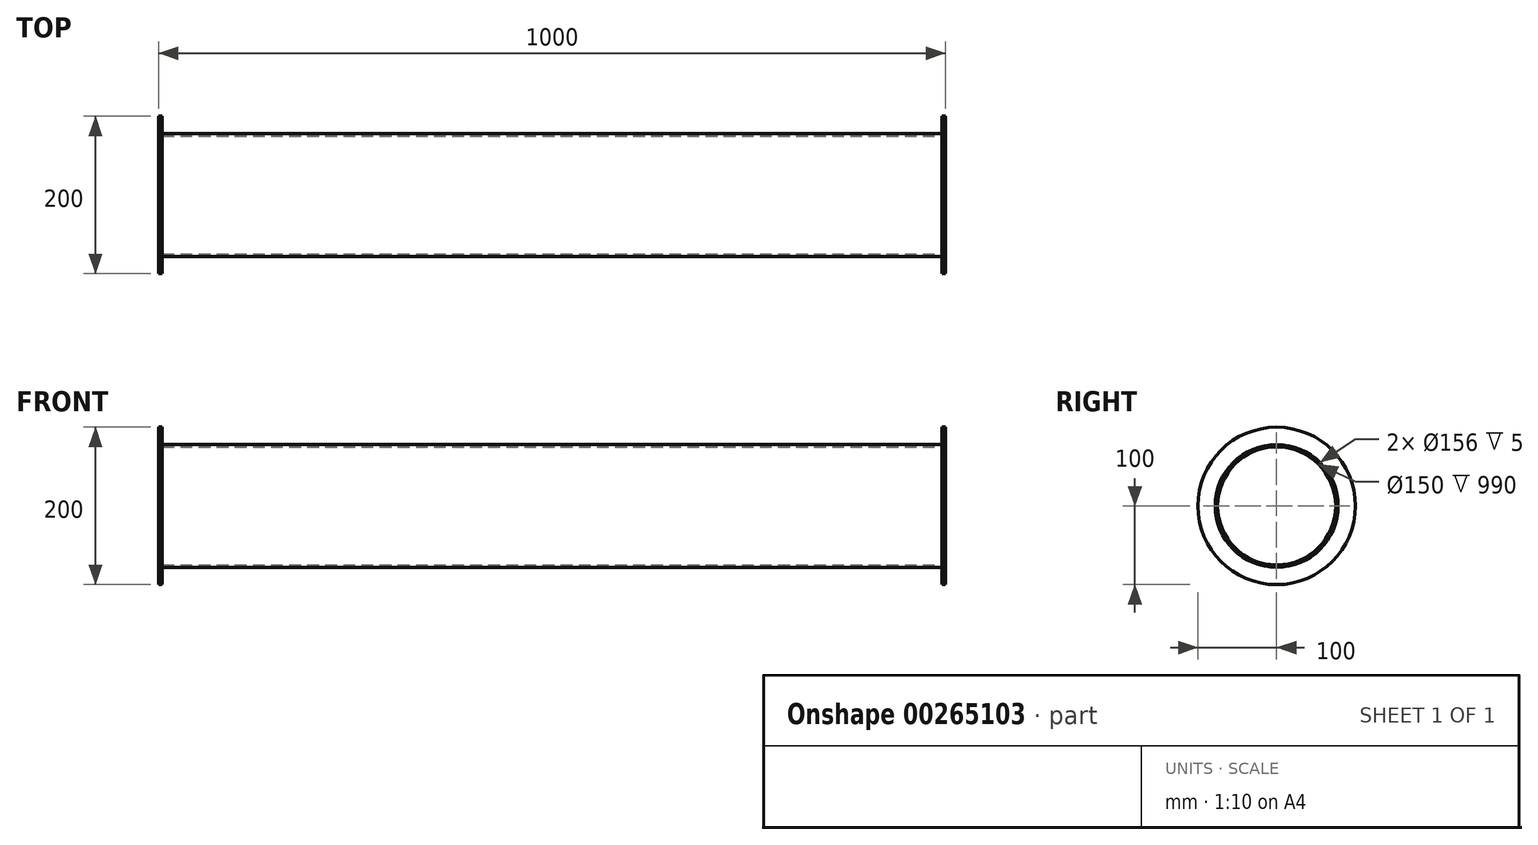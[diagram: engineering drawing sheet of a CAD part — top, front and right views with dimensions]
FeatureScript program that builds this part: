
annotation { "Feature Type Name" : "Feature", "Feature Type Description" : "" }
export const myFeature = defineFeature(function(context is Context, id is Id, definition is map)
    precondition{}
    {
        {
            var Q0;
            Q0=qCreatedBy(makeId("Front.planeOp"),FACE);
            var sketch = newSketch(context, id + "F0", { "sketchPlane" : qUnion([Q0])});
            skLineSegment(sketch, "E0", {"start": v(0, 0) * mm, "end": v(-990, 0) * mm, "construction": true});
            skLineSegment(sketch, "E1.bottom", {"start": v(0, 75) * mm, "end": v(-990, 75) * mm});
            skLineSegment(sketch, "E1.top", {"start": v(0, 78) * mm, "end": v(-990, 78) * mm});
            skLineSegment(sketch, "E1.left", {"start": v(0, 75) * mm, "end": v(0, 78) * mm});
            skLineSegment(sketch, "E1.right", {"start": v(-990, 75) * mm, "end": v(-990, 78) * mm});
            skSolve(sketch);
        }
        {
            var Q0;
            Q0=makeQuery(id+"F0.imprint","IMPRINT",FACE,{"disambiguationData":[TD([[makeQuery(id+"F0.imprint","IMPRINT",EDGE,{"derivedFrom":sQuery(id+"F0.wireOp",EDGE,"E1.bottom")}),-1.0]])]});
            var Q1;
            Q1=sQuery(id+"F0.wireOp",EDGE,"E0");
            revolve(context, id + "F1", {"entities" : qUnion([Q0]), "axis" : qUnion([Q1]), "revolveType" : RevolveType.FULL});
        }
        {
            var Q0;
            Q0=makeQuery(id+"F1.opRevolve","SWEPT_FACE",FACE,{"disambiguationData":[OSD([sQuery(id+"F0.wireOp",EDGE,"E1.right")])]});
            var sketch = newSketch(context, id + "F2", { "sketchPlane" : qUnion([Q0])});
            skCircle(sketch, "E2", {"center": v(0, 0) * mm, "radius": 100 * mm});
            skCircle(sketch, "E3", {"center": v(0, 0) * mm, "radius": 75 * mm});
            skSolve(sketch);
        }
        {
            var Q0;
            Q0=makeQuery(id+"F2.imprint","IMPRINT",FACE,{"disambiguationData":[TD([[makeQuery(id+"F2.imprint","IMPRINT",EDGE,{"derivedFrom":sQuery(id+"F2.wireOp",EDGE,"E2")}),1.0]])]});
            extrude(context, id + "F3", {"entities" : qUnion([Q0]), "depth" : 5 * mm});
        }
        {
            var Q0;
            Q0=makeQuery(id+"F1.opRevolve","SWEPT_FACE",FACE,{"disambiguationData":[OSD([sQuery(id+"F0.wireOp",EDGE,"E1.left")])]});
            var sketch = newSketch(context, id + "F4", { "sketchPlane" : qUnion([Q0])});
            skCircle(sketch, "E4", {"center": v(0, 0) * mm, "radius": 100 * mm});
            skCircle(sketch, "E5", {"center": v(0, 0) * mm, "radius": 75 * mm});
            skSolve(sketch);
        }
        {
            var Q0;
            Q0=makeQuery(id+"F4.imprint","IMPRINT",FACE,{"disambiguationData":[TD([[makeQuery(id+"F4.imprint","IMPRINT",EDGE,{"derivedFrom":sQuery(id+"F4.wireOp",EDGE,"E4")}),1.0]])]});
            extrude(context, id + "F5", {"entities" : qUnion([Q0]), "depth" : 5 * mm});
        }
    });
